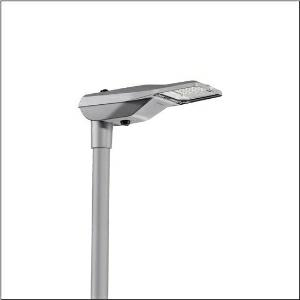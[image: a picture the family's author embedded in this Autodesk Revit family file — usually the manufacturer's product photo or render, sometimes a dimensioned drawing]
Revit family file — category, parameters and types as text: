
# Revit family: streetlight_sl_21_iq_micro___p0_8a_5xe1u31y08cb_2316
name_source: partatom
category: Lighting Fixtures
units: mm (PartAtom-declared; Revit-internal decimal feet)

## family parameters
Cut with Voids When Loaded = No
Host = Face
Light Source = No
Part Type = Normal
Room Calculation Point = No
Round Connector Dimension = Use Diameter
Shared = No

## types (1)
- --- (1 x LED, 2890 lm, 19.1 W, 3000K)
    Apparent Load = 19 VA
    CIE Flux Codes = 33 69 96 100 100
    Color Rendering = 70
    Color Temperature = 3000K
    Default Elevation = 1800 mm
    Description = Streetlight SL 21 iQ micro, mast luminaire, primary light control with lens, of PMMA, primary optical cover: cover, of toughened safety glass, transparent, light distribution: P0.8a, light emission: direct distribution, primary light characteristic: asymmetric, installation type: post-top, side-entry, LED, High Power LED, rated luminous flux: 2.890lm, luminous efficacy: 151lm/W, light colour: 730, colour temperature: 3000K, control gear: iQ-Street Remote, D4i with power reduction, control: pre-setting: logarithmic dimming characteristic, Street-Remote, Auto-Match, Temp-Guard, Lumen-Switch, Night-Set, Smart-Wire, Light-Fading, Desk-Remote (wireless, voltage-free reading and setting of iQ features in the workshop via application-optimized NFC function/RFID function), optimised constant luminous flux control (CLO 2.0), mains connection: 220..240V, AC, 50/60Hz, start of lifetime: 19W, end of service life: 20W, reduction: 9W, luminaire housing, of diecast aluminium, powder-coated, SITECO metallic grey (DB 702S), corrosivity category C5 high according to DIN EN ISO 12944, please order mast flange separately, inclination adjustable: 0°, 5°, 10°, 15°, sealing non-destructively replaceable, multi-level sealing system, length: 528mm, width: 235mm, height: 110mm, mast flange for spigot size: 42mm (side-entry): 5XC10008XM4, 60/48mm (side-entry/post-top): 5XC10108XM2, 76/60mm (side-entry/post-top): 5XC10108XM1, mounting height: 4..8m, Smart Interface below and above, protection rating (complete): IP66, insulation class (complete): insulation class II (safety insulation), certification: CE, ENEC, ENEC+, VDE, impact resistance: IK10, permissible operating ambient temperature for outdoor applications: -40..+50°C, standard-compliant lighting for roads and squares, packaging unit: 1 piece

Light Distribution: P0.8a
    Height = 110 mm
    Lamp = 1 x LED
    Lamp Light Flux = 2890 lm
    Lamp Power = 19.1 W
    Lamp count = 1
    Length = 528 mm
    Luminous efficacy = 151 lm/W
    Manufacturer = Siteco
    ModVariant = No
    Model = 5XE1U31Y08CB
    Number of Poles = 1
    OnlyDefault = Yes
    Power Factor = 1
    Product Name = Streetlight SL 21 iQ micro | P0.8a
    Product group = mast luminaire | pylon top
    ProductGroupID = 6100
    Protection Class = Protection class II
    Protection Degree = IP 66
    RLX_Detail_Level = 1
    RLX_Emergency_Light_Flux = 0 lm
    RLX_Emergency_Type = 0
    RLX_Emergency_Type_DB = No
    RlxData = <blob elided: 98309 chars, md5=32593e42>
    Socket = socket
    Standby Power = 0 W
    System Light Flux = 2890 lm
    System Power = 19 W
    Type Comments = factory setting: luminous flux: 100 % | dim-lin: 254 | 387 mA
    Type Image = l_1007239.jpg
    URL = http://relux.com
    VarID = @adj_080631
    Voltage = 0 V
    Weight = 0.00 kg
    Width = 235 mm

## geometry (parser evidence)
native form markers: Blend x4, Sweep x10
no freeform markers — native parametric forms only
